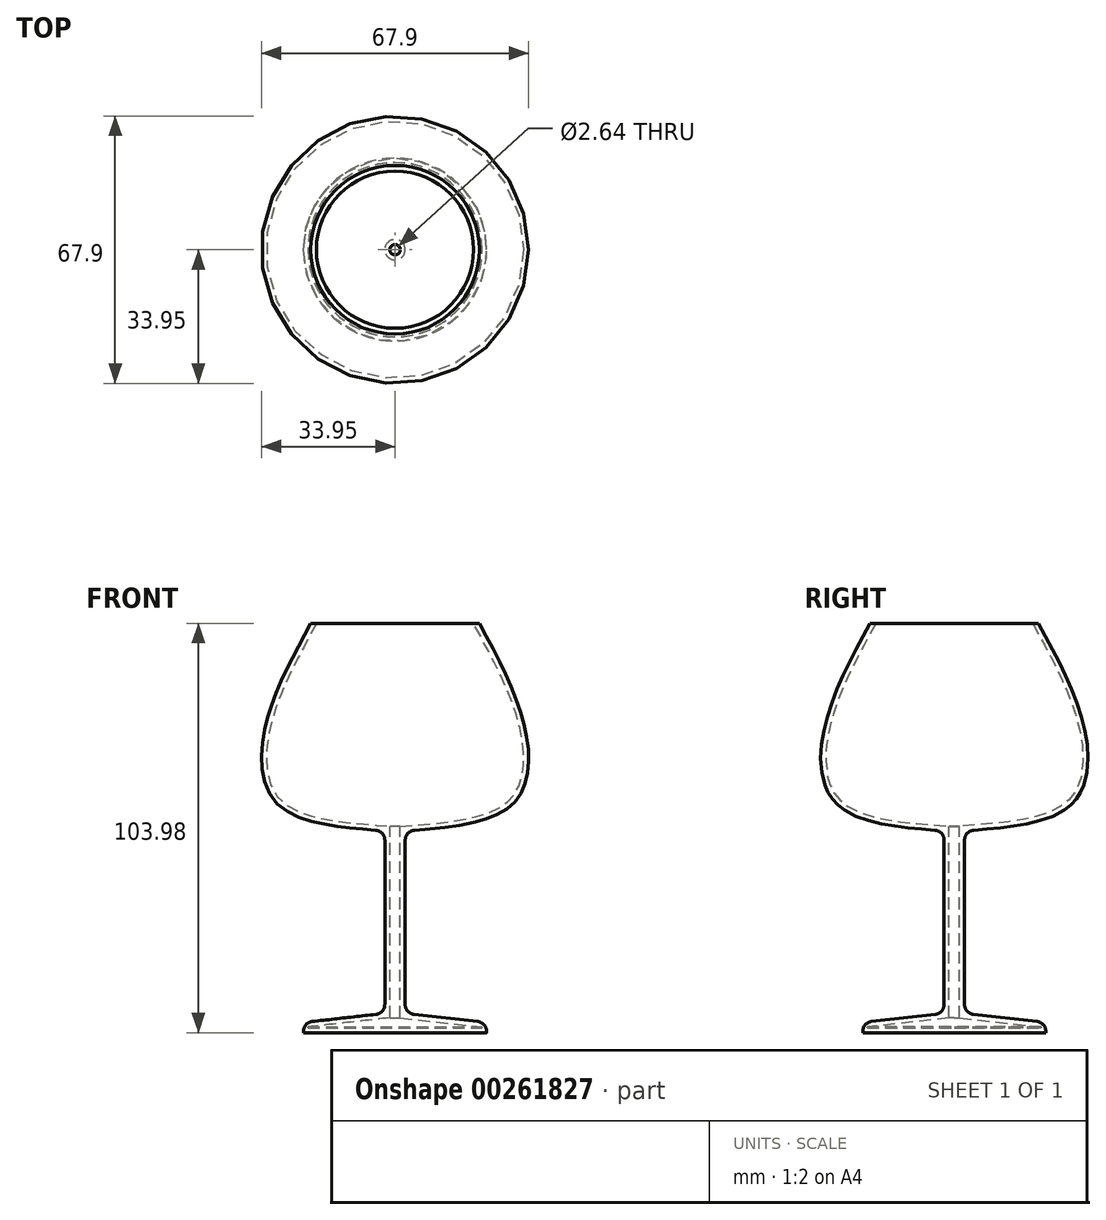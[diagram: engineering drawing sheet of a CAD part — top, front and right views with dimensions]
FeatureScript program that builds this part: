
annotation { "Feature Type Name" : "Feature", "Feature Type Description" : "" }
export const myFeature = defineFeature(function(context is Context, id is Id, definition is map)
    precondition{}
    {
        {
            var Q0;
            Q0=qCreatedBy(makeId("Front.planeOp"),FACE);
            var sketch = newSketch(context, id + "F0", { "sketchPlane" : qUnion([Q0])});
            skLineSegment(sketch, "E0", {"start": v(0, 64.48) * mm, "end": v(0, -67.3) * mm});
            skLineSegment(sketch, "E1", {"start": v(-23.53, -60.24) * mm, "end": v(-2.59, -57.89) * mm});
            skLineSegment(sketch, "E2", {"start": v(-2.59, -57.89) * mm, "end": v(-2.59, -11.53) * mm});
            skFitSpline(sketch, "E3", {"points": [v(-2.59, -11.53) * mm, v(-29.89, -4.7) * mm, v(-33.18, 13.88) * mm, v(-21.41, 41.18) * mm], "startDerivative": vector(-94.06, 7.06) * mm, "endDerivative": vector(41.12, 75.85) * mm});
            skLineSegment(sketch, "E4", {"start": v(-21.41, 41.18) * mm, "end": v(0, 41.18) * mm});
            skLineSegment(sketch, "E5", {"start": v(-2.59, -11.53) * mm, "end": v(0, -11.53) * mm});
            skLineSegment(sketch, "E6", {"start": v(-23.53, -60.24) * mm, "end": v(-23.25, -62.8) * mm});
            skLineSegment(sketch, "E7", {"start": v(-23.25, -62.8) * mm, "end": v(0, -62.8) * mm});
            skSolve(sketch);
        }
        {
            var Q0;
            Q0=makeQuery(id+"F0.imprint","IMPRINT",FACE,{"disambiguationData":[TD([[makeQuery(id+"F0.imprint","IMPRINT",EDGE,{"derivedFrom":sQuery(id+"F0.wireOp",EDGE,"E3")}),-1.0]])]});
            var Q1;
            Q1=makeQuery(id+"F0.imprint","IMPRINT",FACE,{"disambiguationData":[TD([[makeQuery(id+"F0.imprint","IMPRINT",EDGE,{"derivedFrom":sQuery(id+"F0.wireOp",EDGE,"E1")}),-1.0]])]});
            var Q2;
            Q2=sQuery(id+"F0.wireOp",EDGE,"E0");
            revolve(context, id + "F1", {"entities" : qUnion([Q0, Q1]), "axis" : qUnion([Q2]), "revolveType" : RevolveType.FULL});
        }
        {
            var Q0;
            Q0=makeQuery(id+"F1.opRevolve","SWEPT_FACE",FACE,{"disambiguationData":[OSD([sQuery(id+"F0.wireOp",EDGE,"E4")])]});
            shell(context, id + "F2", {"entities" : qUnion([Q0]), "thickness" : 1.27 * mm});
        }
        {
            var Q0;
            Q0=makeQuery(id+"F1.opRevolve","SWEPT_EDGE",EDGE,{"disambiguationData":[OSD([sQuery(id+"F0.wireOp",EDGE,"E1"),sQuery(id+"F0.wireOp",EDGE,"E6")])]});
            var Q1;
            Q1=makeQuery(id+"F1.opRevolve","SWEPT_EDGE",EDGE,{"disambiguationData":[OSD([sQuery(id+"F0.wireOp",EDGE,"E1"),sQuery(id+"F0.wireOp",EDGE,"E2")])]});
            var Q2;
            Q2=makeQuery(id+"F1.opRevolve","SWEPT_EDGE",EDGE,{"disambiguationData":[OSD([sQuery(id+"F0.wireOp",EDGE,"E2"),sQuery(id+"F0.wireOp",EDGE,"E3"),sQuery(id+"F0.wireOp",EDGE,"E5")])]});
            fillet(context, id + "F3", {"entities" : qUnion([Q0, Q1, Q2]), "radius" : 2.54 * mm, "tangentPropagation" : true, "allowEdgeOverflow" : false});
        }
    });
